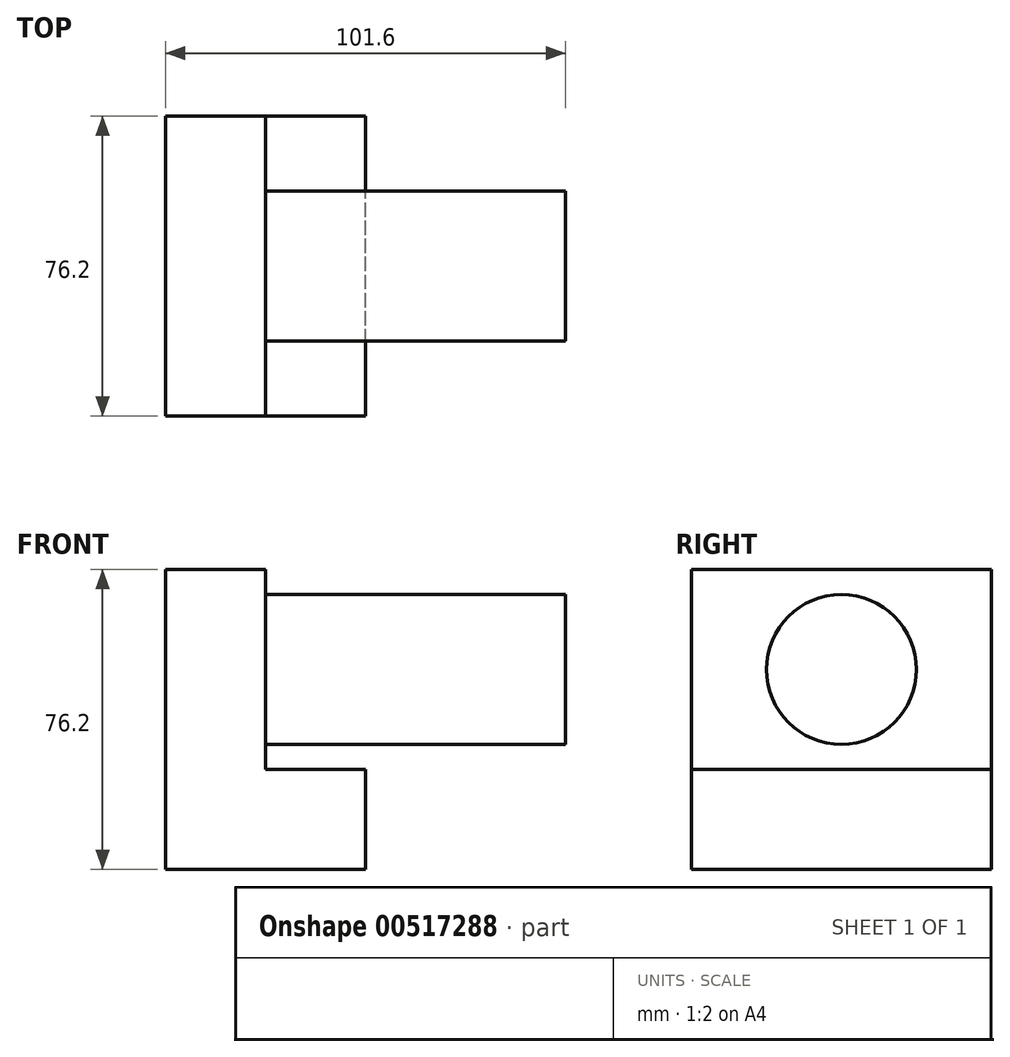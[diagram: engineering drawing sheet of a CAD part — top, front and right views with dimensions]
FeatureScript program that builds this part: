
annotation { "Feature Type Name" : "Feature", "Feature Type Description" : "" }
export const myFeature = defineFeature(function(context is Context, id is Id, definition is map)
    precondition{}
    {
        {
            var Q0;
            Q0=qCreatedBy(makeId("Front.planeOp"),FACE);
            var sketch = newSketch(context, id + "F0", { "sketchPlane" : qUnion([Q0])});
            skLineSegment(sketch, "E0", {"start": v(0, 0) * mm, "end": v(25.4, 0) * mm});
            skLineSegment(sketch, "E1", {"start": v(25.4, 0) * mm, "end": v(25.4, -25.4) * mm});
            skLineSegment(sketch, "E2", {"start": v(25.4, -25.4) * mm, "end": v(-25.4, -25.4) * mm});
            skLineSegment(sketch, "E3", {"start": v(-25.4, -25.4) * mm, "end": v(-25.4, 50.8) * mm});
            skLineSegment(sketch, "E4", {"start": v(-25.4, 50.8) * mm, "end": v(0, 50.8) * mm});
            skLineSegment(sketch, "E5", {"start": v(0, 50.8) * mm, "end": v(0, 0) * mm});
            skSolve(sketch);
        }
        {
            var Q0;
            Q0 = qSketchRegion(id + "F0", true);
            extrude(context, id + "F1", {"entities" : qUnion([Q0]), "depth" : 76.2 * mm, "offsetDistance" : 25.4 * mm});
        }
        {
            var Q0;
            Q0=makeQuery(id+"F1.opExtrude","SWEPT_FACE",FACE,{"disambiguationData":[OSD([sQuery(id+"F0.wireOp",EDGE,"E5")])]});
            var sketch = newSketch(context, id + "F2", { "sketchPlane" : qUnion([Q0])});
            skLineSegment(sketch, "E6", {"start": v(-38.1, 50.8) * mm, "end": v(-38.1, 0) * mm, "construction": true});
            skLineSegment(sketch, "E7", {"start": v(-76.2, 25.4) * mm, "end": v(0, 25.4) * mm, "construction": true});
            skLineSegment(sketch, "E8", {"start": v(0, 25.4) * mm, "end": v(-38.1, 25.4) * mm});
            skCircle(sketch, "E9", {"center": v(-38.1, 25.4) * mm, "radius": 19.05 * mm});
            skSolve(sketch);
        }
        {
            var Q0;
            Q0 = qSketchRegion(id + "F2", true);
            extrude(context, id + "F3", {"entities" : qUnion([Q0]), "operationType" : NewBodyOperationType.ADD, "depth" : 76.2 * mm, "offsetDistance" : 25.4 * mm});
        }
    });
